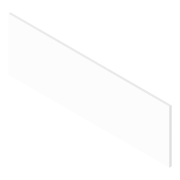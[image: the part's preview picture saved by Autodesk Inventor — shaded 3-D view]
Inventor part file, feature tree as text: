
AUTODESK INVENTOR PART (.ipt)
format: ipt  version: 2022 (Build 260153000, 153)  size: 76,800 bytes
history: native  units: mm
features: extrude x1, plane x1, sketch x1
ambient origin geometry x8: Origin, YZ Plane, XZ Plane, XY Plane, X Axis, Y Axis, Z Axis, Center Point
bodies: Volumenkörper1 (feature_tree)
feature tree (3):
  extrude  "Extrusion1"  Depth=25.0mm
  plane  "Arbeitsebene1"
  sketch  "Skizze1"  dims[d0=76.0mm d1=25.0mm d2=1.0mm d3=0.0mm]
